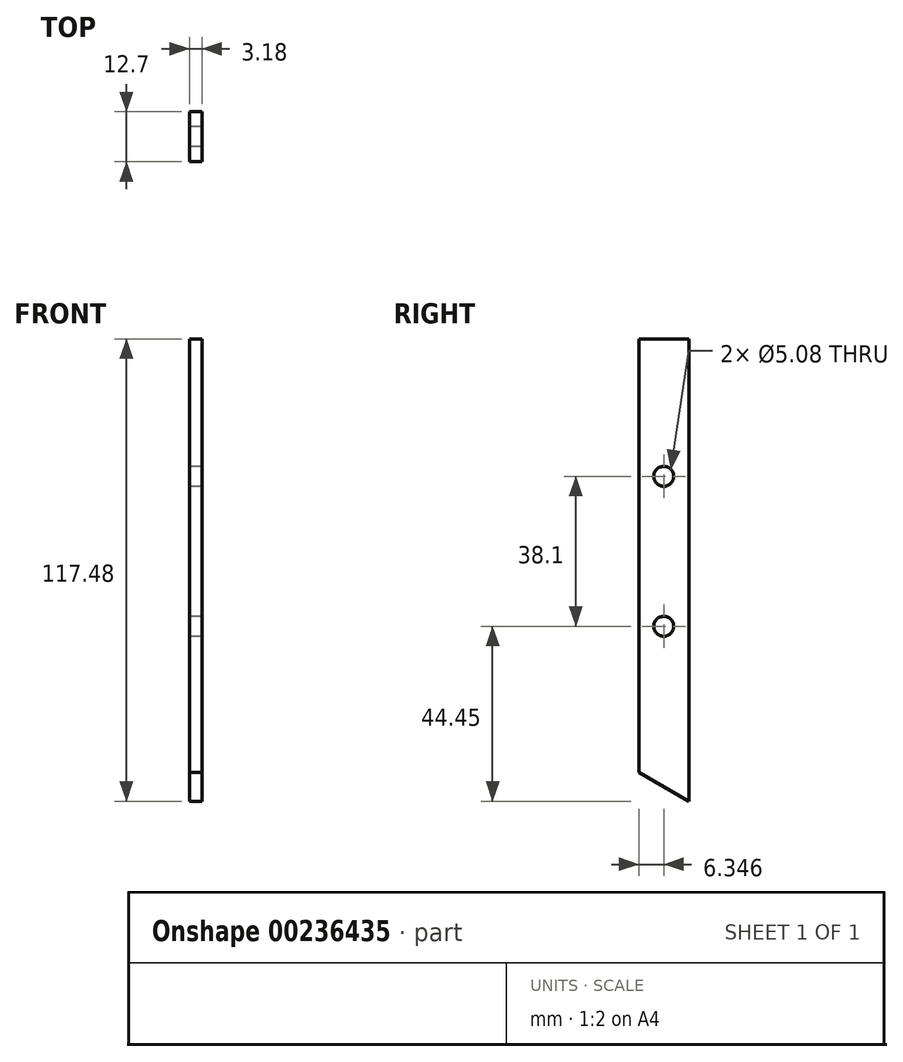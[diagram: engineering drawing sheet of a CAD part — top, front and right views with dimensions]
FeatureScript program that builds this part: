
annotation { "Feature Type Name" : "Feature", "Feature Type Description" : "" }
export const myFeature = defineFeature(function(context is Context, id is Id, definition is map)
    precondition{}
    {
        {
            var Q0;
            Q0=qCreatedBy(makeId("Right.planeOp"),FACE);
            var sketch = newSketch(context, id + "F0", { "sketchPlane" : qUnion([Q0])});
            skLineSegment(sketch, "E0", {"start": v(2.18, 80.72) * mm, "end": v(2.18, -36.76) * mm});
            skLineSegment(sketch, "E1", {"start": v(2.18, -36.76) * mm, "end": v(-10.52, -29.43) * mm});
            skLineSegment(sketch, "E2", {"start": v(-10.52, 80.72) * mm, "end": v(-10.52, -29.43) * mm});
            skCircle(sketch, "E3", {"center": v(-4.17, 45.8) * mm, "radius": 2.54 * mm});
            skCircle(sketch, "E4", {"center": v(-4.17, 7.7) * mm, "radius": 2.54 * mm});
            skLineSegment(sketch, "E5", {"start": v(-10.52, 80.72) * mm, "end": v(2.18, 80.72) * mm});
            skSolve(sketch);
        }
        {
            var Q0;
            Q0 = qSketchRegion(id + "F0", true);
            extrude(context, id + "F1", {"entities" : qUnion([Q0]), "depth" : 3.17 * mm});
        }
    });
